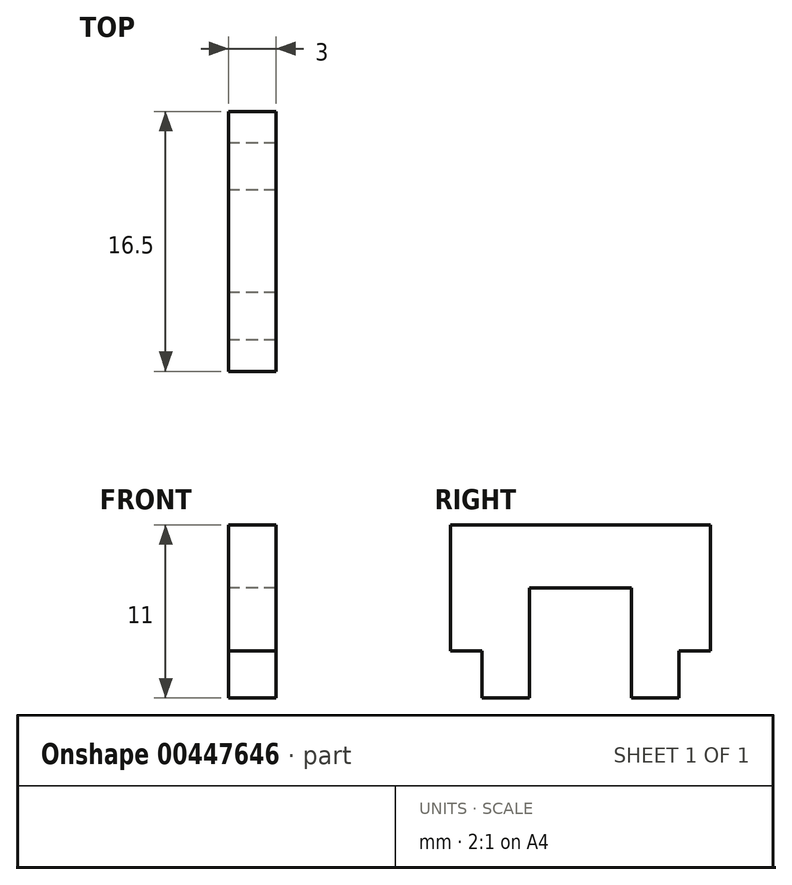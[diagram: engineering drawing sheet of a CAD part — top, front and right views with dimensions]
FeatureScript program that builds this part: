
annotation { "Feature Type Name" : "Feature", "Feature Type Description" : "" }
export const myFeature = defineFeature(function(context is Context, id is Id, definition is map)
    precondition{}
    {
        {
            var Q0;
            Q0=qCreatedBy(makeId("Right.planeOp"),FACE);
            var sketch = newSketch(context, id + "F0", { "sketchPlane" : qUnion([Q0])});
            skLineSegment(sketch, "E0.bottom", {"start": v(3.25, -2) * mm, "end": v(-3.25, -2) * mm});
            skLineSegment(sketch, "E0.top", {"start": v(3.25, 2) * mm, "end": v(-3.25, 2) * mm});
            skLineSegment(sketch, "E0.left", {"start": v(3.25, -2) * mm, "end": v(3.25, 2) * mm});
            skLineSegment(sketch, "E0.right", {"start": v(-3.25, -2) * mm, "end": v(-3.25, 2) * mm});
            skPoint(sketch, "E0.middle", {"position": v(0, 0) * mm});
            skLineSegment(sketch, "E1.bottom", {"start": v(-8.25, -6) * mm, "end": v(-3.25, -6) * mm});
            skLineSegment(sketch, "E1.top", {"start": v(-8.25, 2) * mm, "end": v(-3.25, 2) * mm});
            skLineSegment(sketch, "E1.left", {"start": v(-8.25, -6) * mm, "end": v(-8.25, 2) * mm});
            skLineSegment(sketch, "E1.right", {"start": v(-3.25, -6) * mm, "end": v(-3.25, 2) * mm});
            skPoint(sketch, "E1.middle", {"position": v(-5.75, -2) * mm});
            skLineSegment(sketch, "E2.bottom", {"start": v(-6.25, -9) * mm, "end": v(-3.25, -9) * mm});
            skLineSegment(sketch, "E2.top", {"start": v(-6.25, -6) * mm, "end": v(-3.25, -6) * mm});
            skLineSegment(sketch, "E2.left", {"start": v(-6.25, -9) * mm, "end": v(-6.25, -6) * mm});
            skLineSegment(sketch, "E2.right", {"start": v(-3.25, -9) * mm, "end": v(-3.25, -6) * mm});
            skPoint(sketch, "E2.middle", {"position": v(-4.75, -7.5) * mm});
            skLineSegment(sketch, "E3.bottom", {"start": v(8.25, -6) * mm, "end": v(3.25, -6) * mm});
            skLineSegment(sketch, "E3.top", {"start": v(8.25, 2) * mm, "end": v(3.25, 2) * mm});
            skLineSegment(sketch, "E3.left", {"start": v(8.25, -6) * mm, "end": v(8.25, 2) * mm});
            skLineSegment(sketch, "E3.right", {"start": v(3.25, -6) * mm, "end": v(3.25, 2) * mm});
            skPoint(sketch, "E3.middle", {"position": v(5.75, -2) * mm});
            skLineSegment(sketch, "E4.bottom", {"start": v(6.25, -9) * mm, "end": v(3.25, -9) * mm});
            skLineSegment(sketch, "E4.top", {"start": v(6.25, -6) * mm, "end": v(3.25, -6) * mm});
            skLineSegment(sketch, "E4.left", {"start": v(6.25, -9) * mm, "end": v(6.25, -6) * mm});
            skLineSegment(sketch, "E4.right", {"start": v(3.25, -9) * mm, "end": v(3.25, -6) * mm});
            skPoint(sketch, "E4.middle", {"position": v(4.75, -7.5) * mm});
            skSolve(sketch);
        }
        {
            var Q0;
            Q0 = qSketchRegion(id + "F0", true);
            extrude(context, id + "F1", {"entities" : qUnion([Q0]), "depth" : 3 * mm});
        }
    });
